# Revit family: Door-NanaWall-NW-Aluminum-640
name_source: partatom
category: Doors
units: mm (PartAtom-declared; Revit-internal decimal feet)

## family parameters
Always vertical = Yes
Cut with Voids When Loaded = No
Host = Wall
OmniClass Number = 23.30.10.17.17
OmniClass Title = Folding Doors and Grilles
Room Calculation Point = No
Shared = No

## types (1)
- Standard
    04 CSI = 08 41 13
    95 CSI = 8411
    Assembly Code = B2050.4010
    Cost Info = https://www.nanawall.com
    Description = Standard Thermally Broken Aluminum Framed Folding system
    Disclaimer = Please note that the Revit model is for schematic purposes only.  To obtain a detailed 3D model, please go to the NanaWall's configurator at www.nanawall.com.
    Engineering Details URL = https://www.nanawall.com
    Exterior Wall Offset = 5"
    Filler = Rubber - NanaWall - Black
    Glass Material = Glass - NanaWall - Generic
    Installation and Service URL = http://www.nanawall.com
    Manufacturer = NanaWall Systems, Inc.
    Manufacturer Fax = (415) 383-0312
    Model = NW Aluminum 640 (SL64)
    Performance URL = https://www.nanawall.com
    Product Page URL = https://www.nanawall.com
    Sash = Metal - NanaWall - Aluminum
    Sills Available = Raised, Low Profile Saddle, Flush
    Subcategory = Folding Door
    Thickness = 2 5/8"
    U Value = 0.27
    URL = http://www.nanawall.com
    Wall Closure = By host
    Warranty URL = http://www.nanawall.com

## geometry (parser evidence)
native form markers: Sweep x35
no freeform markers — native parametric forms only
